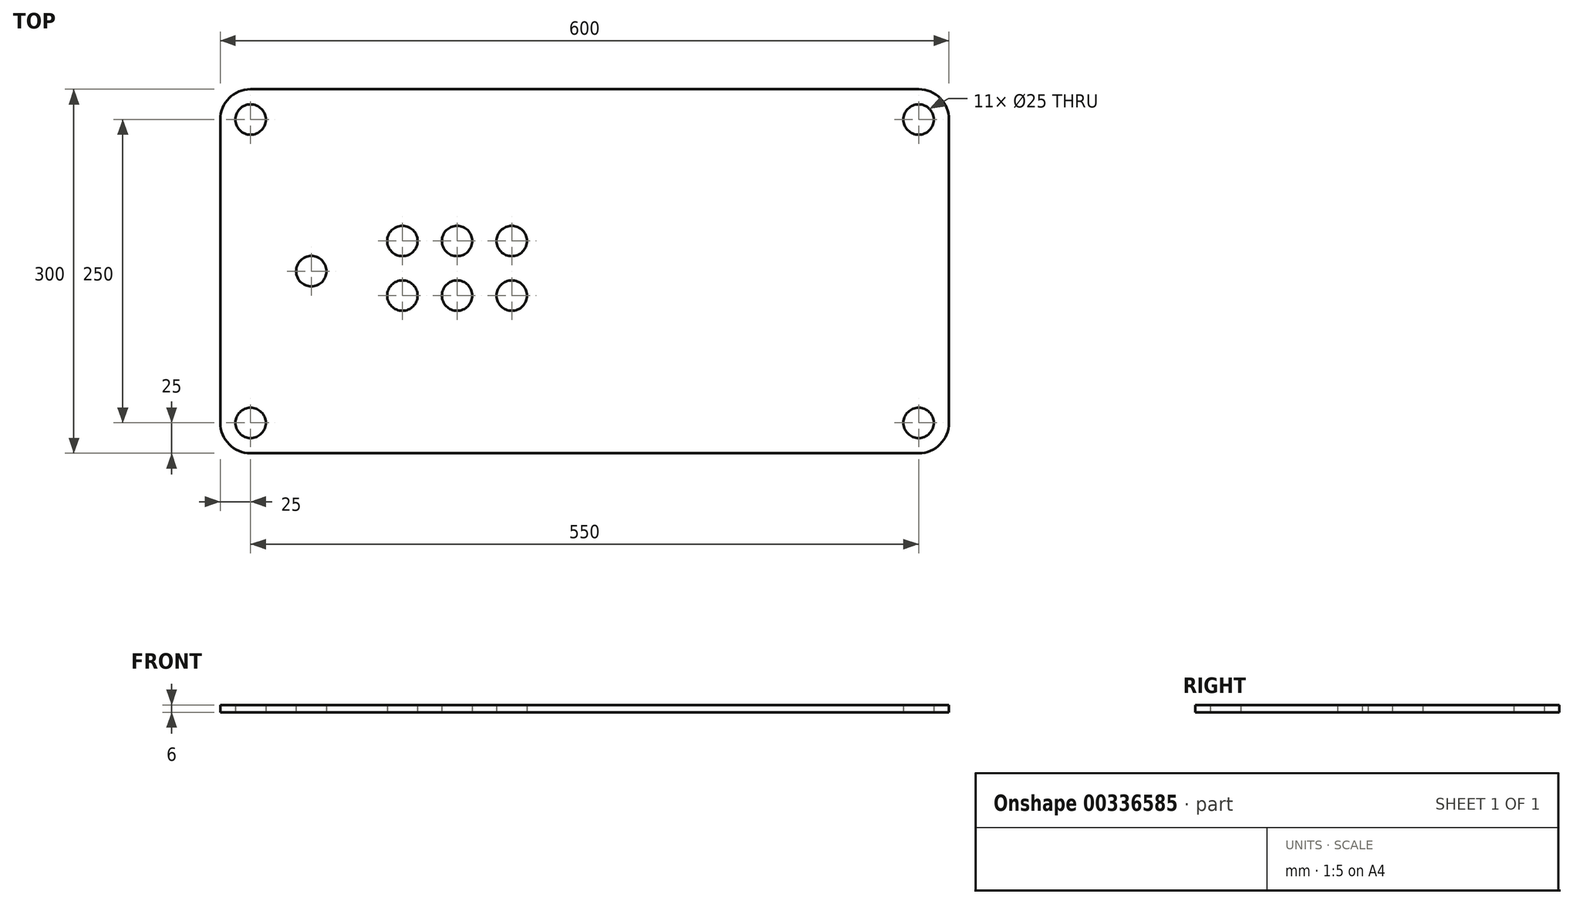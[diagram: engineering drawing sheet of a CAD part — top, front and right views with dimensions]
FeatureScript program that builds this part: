
annotation { "Feature Type Name" : "Feature", "Feature Type Description" : "" }
export const myFeature = defineFeature(function(context is Context, id is Id, definition is map)
    precondition{}
    {
        {
            var Q0;
            Q0=qCreatedBy(makeId("Top.planeOp"),FACE);
            var sketch = newSketch(context, id + "F0", { "sketchPlane" : qUnion([Q0])});
            skLineSegment(sketch, "E0.bottom", {"start": v(275, -150) * mm, "end": v(-275, -150) * mm});
            skLineSegment(sketch, "E0.top", {"start": v(275, 150) * mm, "end": v(-275, 150) * mm});
            skLineSegment(sketch, "E0.left", {"start": v(300, -125) * mm, "end": v(300, 125) * mm});
            skLineSegment(sketch, "E0.right", {"start": v(-300, -125) * mm, "end": v(-300, 125) * mm});
            skPoint(sketch, "E0.middle", {"position": v(0, 0) * mm});
            skPoint(sketch, "E1.visualSharp", {"position": v(-300, 150) * mm});
            skArc(sketch, "E1.filletArc", {"start": v(-275, 150) * mm, "mid": v(-292.68, 142.68) * mm, "end": v(-300, 125) * mm});
            skPoint(sketch, "E2.visualSharp", {"position": v(-300, -150) * mm});
            skArc(sketch, "E2.filletArc", {"start": v(-300, -125) * mm, "mid": v(-292.68, -142.68) * mm, "end": v(-275, -150) * mm});
            skPoint(sketch, "E3.visualSharp", {"position": v(300, 150) * mm});
            skArc(sketch, "E3.filletArc", {"start": v(300, 125) * mm, "mid": v(292.68, 142.68) * mm, "end": v(275, 150) * mm});
            skPoint(sketch, "E4.visualSharp", {"position": v(300, -150) * mm});
            skArc(sketch, "E4.filletArc", {"start": v(275, -150) * mm, "mid": v(292.68, -142.68) * mm, "end": v(300, -125) * mm});
            skPoint(sketch, "E5", {"position": v(-60, 24.9) * mm});
            skPoint(sketch, "E6", {"position": v(-60, -20.1) * mm});
            skPoint(sketch, "E7", {"position": v(-105, -20.1) * mm});
            skPoint(sketch, "E8", {"position": v(-150, -20.1) * mm});
            skPoint(sketch, "E9", {"position": v(-150, 24.9) * mm});
            skPoint(sketch, "E10", {"position": v(-105, 24.9) * mm});
            skPoint(sketch, "E11", {"position": v(-174.1, 165.8) * mm});
            skPoint(sketch, "E12", {"position": v(-170.27, 158.14) * mm});
            skPoint(sketch, "E13", {"position": v(-225, 0) * mm});
            skSolve(sketch);
        }
        {
            var Q0;
            Q0=makeQuery(id+"F0.imprint","IMPRINT",FACE,{"disambiguationData":[TD([[makeQuery(id+"F0.imprint","IMPRINT",EDGE,{"derivedFrom":sQuery(id+"F0.wireOp",EDGE,"E0.bottom")}),-1.0]])]});
            extrude(context, id + "F1", {"entities" : qUnion([Q0]), "depth" : 6 * mm});
        }
        {
            var Q0;
            Q0=sQuery(id+"F0.wireOp",VERTEX,"E2.filletArc.center");
            var Q1;
            Q1=makeQuery(id+"F1.opExtrude","SWEPT_BODY",BODY,{"disambiguationData":[OSD([sQuery(id+"F0.wireOp",EDGE,"E0.bottom"),sQuery(id+"F0.wireOp",EDGE,"E0.top"),sQuery(id+"F0.wireOp",EDGE,"E0.left"),sQuery(id+"F0.wireOp",EDGE,"E0.right"),sQuery(id+"F0.wireOp",EDGE,"E1.filletArc"),sQuery(id+"F0.wireOp",EDGE,"E2.filletArc"),sQuery(id+"F0.wireOp",EDGE,"E3.filletArc"),sQuery(id+"F0.wireOp",EDGE,"E4.filletArc")])]});
            hole(context, id + "F2", {"style" : HoleStyle.SIMPLE, "endStyle" : HoleEndStyle.THROUGH, "oppositeDirection" : true, "holeDiameter" : 25 * mm, "tappedDepth" : 12 * mm, "tapClearance" : 3, "locations" : qUnion([Q0]), "scope" : qUnion([Q1])});
        }
        {
            var Q0;
            Q0=sQuery(id+"F0.wireOp",VERTEX,"E1.filletArc.center");
            var Q1;
            Q1=sQuery(id+"F0.wireOp",VERTEX,"E4.filletArc.center");
            var Q2;
            Q2=makeQuery(id+"F1.opExtrude","SWEPT_BODY",BODY,{"disambiguationData":[OSD([sQuery(id+"F0.wireOp",EDGE,"E0.bottom"),sQuery(id+"F0.wireOp",EDGE,"E0.top"),sQuery(id+"F0.wireOp",EDGE,"E0.left"),sQuery(id+"F0.wireOp",EDGE,"E0.right"),sQuery(id+"F0.wireOp",EDGE,"E1.filletArc"),sQuery(id+"F0.wireOp",EDGE,"E2.filletArc"),sQuery(id+"F0.wireOp",EDGE,"E3.filletArc"),sQuery(id+"F0.wireOp",EDGE,"E4.filletArc")])]});
            hole(context, id + "F3", {"style" : HoleStyle.SIMPLE, "endStyle" : HoleEndStyle.THROUGH, "oppositeDirection" : true, "holeDiameter" : 25 * mm, "tappedDepth" : 12 * mm, "tapClearance" : 3, "locations" : qUnion([Q0, Q1]), "scope" : qUnion([Q2])});
        }
        {
            var Q0;
            Q0=sQuery(id+"F0.wireOp",VERTEX,"E3.filletArc.center");
            var Q1;
            Q1=makeQuery(id+"F1.opExtrude","SWEPT_BODY",BODY,{"disambiguationData":[OSD([sQuery(id+"F0.wireOp",EDGE,"E0.bottom"),sQuery(id+"F0.wireOp",EDGE,"E0.top"),sQuery(id+"F0.wireOp",EDGE,"E0.left"),sQuery(id+"F0.wireOp",EDGE,"E0.right"),sQuery(id+"F0.wireOp",EDGE,"E1.filletArc"),sQuery(id+"F0.wireOp",EDGE,"E2.filletArc"),sQuery(id+"F0.wireOp",EDGE,"E3.filletArc"),sQuery(id+"F0.wireOp",EDGE,"E4.filletArc")])]});
            hole(context, id + "F4", {"style" : HoleStyle.SIMPLE, "endStyle" : HoleEndStyle.THROUGH, "oppositeDirection" : true, "holeDiameter" : 25 * mm, "tappedDepth" : 12 * mm, "tapClearance" : 3, "locations" : qUnion([Q0]), "scope" : qUnion([Q1])});
        }
        {
            var Q0;
            Q0=sQuery(id+"F0.wireOp",VERTEX,"E9");
            var Q1;
            Q1=sQuery(id+"F0.wireOp",VERTEX,"E10");
            var Q2;
            Q2=sQuery(id+"F0.wireOp",VERTEX,"E5");
            var Q3;
            Q3=sQuery(id+"F0.wireOp",VERTEX,"E6");
            var Q4;
            Q4=sQuery(id+"F0.wireOp",VERTEX,"E7");
            var Q5;
            Q5=sQuery(id+"F0.wireOp",VERTEX,"E8");
            var Q6;
            Q6=sQuery(id+"F0.wireOp",VERTEX,"E13");
            var Q7;
            Q7=makeQuery(id+"F1.opExtrude","SWEPT_BODY",BODY,{"disambiguationData":[OSD([sQuery(id+"F0.wireOp",EDGE,"E0.bottom"),sQuery(id+"F0.wireOp",EDGE,"E0.top"),sQuery(id+"F0.wireOp",EDGE,"E0.left"),sQuery(id+"F0.wireOp",EDGE,"E0.right"),sQuery(id+"F0.wireOp",EDGE,"E1.filletArc"),sQuery(id+"F0.wireOp",EDGE,"E2.filletArc"),sQuery(id+"F0.wireOp",EDGE,"E3.filletArc"),sQuery(id+"F0.wireOp",EDGE,"E4.filletArc")])]});
            hole(context, id + "F5", {"style" : HoleStyle.SIMPLE, "endStyle" : HoleEndStyle.THROUGH, "oppositeDirection" : true, "holeDiameter" : 25 * mm, "tappedDepth" : 12 * mm, "tapClearance" : 3, "locations" : qUnion([Q0, Q1, Q2, Q3, Q4, Q5, Q6]), "scope" : qUnion([Q7])});
        }
    });
